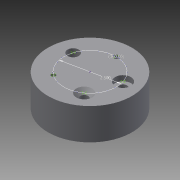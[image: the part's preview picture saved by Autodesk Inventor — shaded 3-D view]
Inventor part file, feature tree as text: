
AUTODESK INVENTOR PART (.ipt)
format: ipt  version: 2015 (Build 190159000, 159)  size: 102,400 bytes
history: native  units: in
note: dims shown in document units (in); Inventor stores cm internally (conversion verified against a paired STEP export)
features: hole x5, sketch x2, extrude x1
ambient origin geometry x8: Origin, YZ Plane, XZ Plane, XY Plane, X Axis, Y Axis, Z Axis, Center Point
bodies: Solid1 (feature_tree)
feature tree (8):
  extrude  "Extrusion1"  Depth=1.5in TaperAngle=0.0deg
  sketch  "Sketch2"  dims[d4=2.5in d5=1.9685in d7=360.0deg d9=0.25in d10=0.75in d11=0.375in d12=0.25in d13=0.5635in d14=1.625in d15=0.8108in d16=0.375in d17=0.75in d18=0.75in d19=0.25in d20=0.5635in d21=1.625in d22=0.8108in d23=0.375in d24=0.75in d25=0.75in d26=0.25in d27=0.5635in d28=1.625in d29=0.8108in d30=0.196in d31=0.5in d32=0.75in d33=0.25in d34=0.5635in d35=0.75in d36=0.8108in d37=0.531in d38=0.5in d39=0.875in d40=0.364in d41=0.5635in d42=0.75in d43=0.8108in]
  hole  "Hole1"  [1 undecoded]
  hole  "Hole2"  [1 undecoded]
  hole  "Hole3"  [1 undecoded]
  hole  "Hole4"  [1 undecoded]
  hole  "Hole5"  [1 undecoded]
  sketch  "Sketch1"  dims[d0=4.0in d2=1.5in d3=0.0in]
note: 5 required parameter values undecoded (feature->parameter linkage not recoverable at this tier; creation-order binding heuristic only, values carry confidence <= 0.55)
